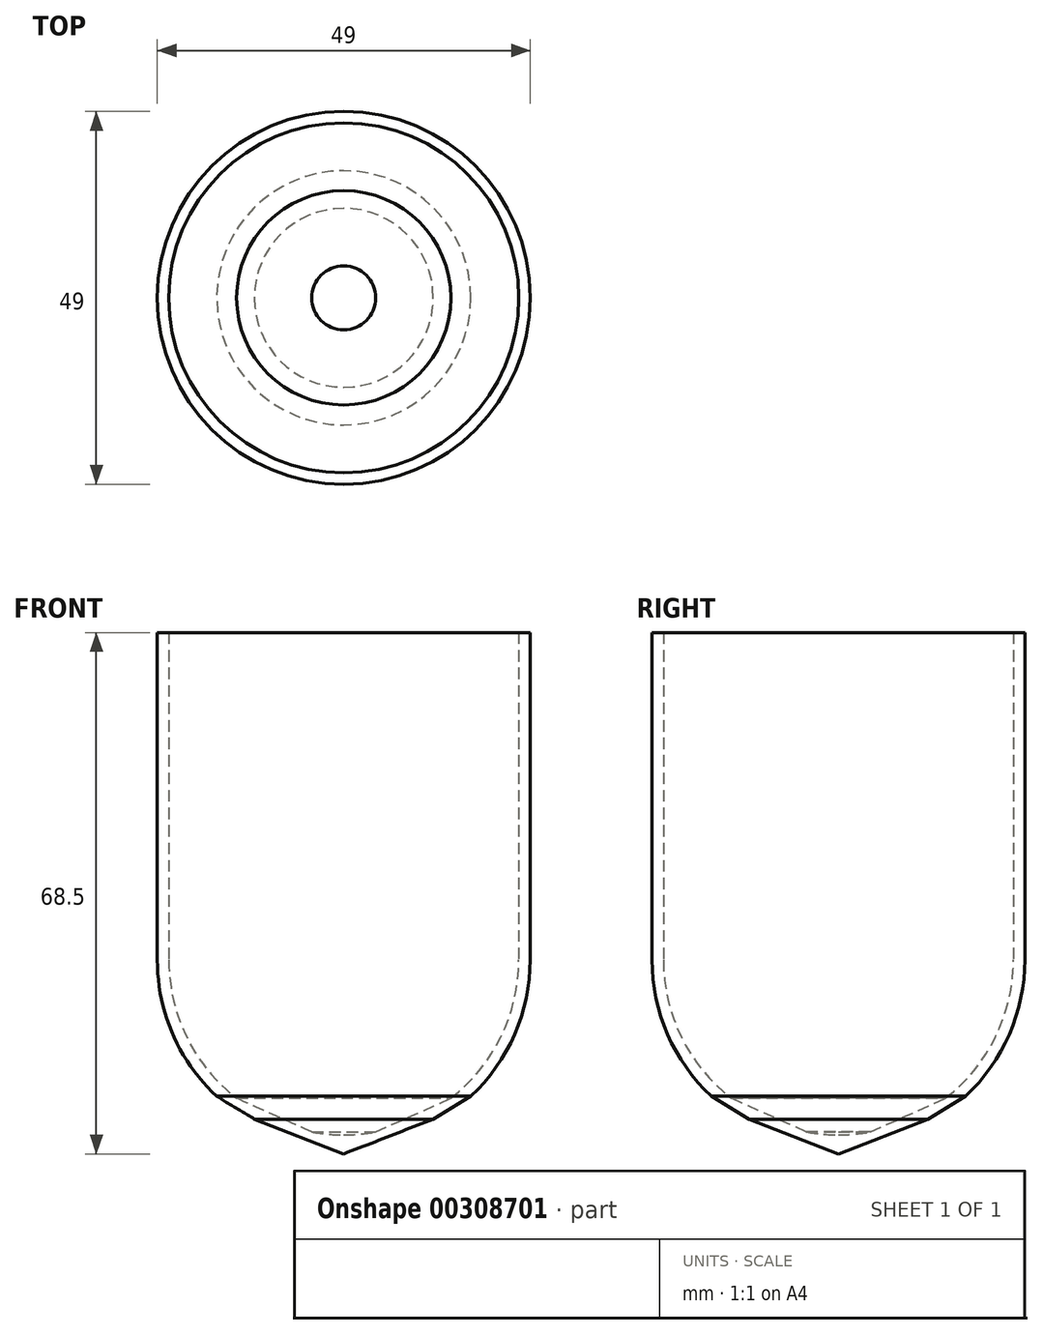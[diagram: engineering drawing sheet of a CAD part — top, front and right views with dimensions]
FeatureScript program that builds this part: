
annotation { "Feature Type Name" : "Feature", "Feature Type Description" : "" }
export const myFeature = defineFeature(function(context is Context, id is Id, definition is map)
    precondition{}
    {
        {
            var Q0;
            Q0=qCreatedBy(makeId("Front.planeOp"),FACE);
            var sketch = newSketch(context, id + "F0", { "sketchPlane" : qUnion([Q0])});
            skLineSegment(sketch, "E0", {"start": v(0, 0) * mm, "end": v(23, 0) * mm, "construction": true});
            skArc(sketch, "E1", {"start": v(0, -23) * mm, "mid": v(16.26, -16.26) * mm, "end": v(23, 0) * mm});
            skArc(sketch, "E2.0", {"start": v(0, -24.5) * mm, "mid": v(17.32, -17.32) * mm, "end": v(24.5, 0) * mm});
            skLineSegment(sketch, "E3", {"start": v(0, -23) * mm, "end": v(0, -24.5) * mm});
            skLineSegment(sketch, "E4", {"start": v(23, 0) * mm, "end": v(24.5, 0) * mm, "construction": true});
            skLineSegment(sketch, "E5", {"start": v(0, -23) * mm, "end": v(0, 0) * mm, "construction": true});
            skLineSegment(sketch, "E6", {"start": v(0, 0) * mm, "end": v(0, 48) * mm, "construction": true});
            skLineSegment(sketch, "E7", {"start": v(23, 0) * mm, "end": v(23, 48) * mm});
            skLineSegment(sketch, "E8", {"start": v(23, 48) * mm, "end": v(24.5, 48) * mm, "construction": true});
            skLineSegment(sketch, "E9", {"start": v(24.5, 48) * mm, "end": v(24.5, 0) * mm});
            skLineSegment(sketch, "E10", {"start": v(24.5, 0) * mm, "end": v(25.5, 0) * mm, "construction": true});
            skLineSegment(sketch, "E11", {"start": v(25.5, 0) * mm, "end": v(32.5, 0) * mm, "construction": true});
            skLineSegment(sketch, "E12", {"start": v(24.5, 48) * mm, "end": v(24.5, 43) * mm});
            skLineSegment(sketch, "E13", {"start": v(24.5, 43) * mm, "end": v(23, 43) * mm});
            skLineSegment(sketch, "E14", {"start": v(0, -24.5) * mm, "end": v(0, -25.5) * mm});
            skLineSegment(sketch, "E15", {"start": v(0, -25.5) * mm, "end": v(11.76, -20.92) * mm});
            skLineSegment(sketch, "E16", {"start": v(11.76, -20.92) * mm, "end": v(16.7, -17.92) * mm});
            skLineSegment(sketch, "E17", {"start": v(4.2, -22.61) * mm, "end": v(14.08, -18.19) * mm});
            skSolve(sketch);
        }
        {
            var Q0;
            {var subQ0=sQuery(id+"F0.wireOp",EDGE,"E17");Q0=makeQuery(id+"F0.imprint","IMPRINT",FACE,{"disambiguationData":[TD([[makeQuery(id+"F0.imprint","IMPRINT",EDGE,{"derivedFrom":subQ0}),-1.0]])]});}
            var Q1;
            {var subQ5=sQuery(id+"F0.wireOp",EDGE,"E3");Q1=makeQuery(id+"F0.imprint","IMPRINT",FACE,{"disambiguationData":[TD([[makeQuery(id+"F0.imprint","IMPRINT",EDGE,{"derivedFrom":subQ5}),1.0]])]});}
            var Q2;
            {var subQ0=sQuery(id+"F0.wireOp",EDGE,"E14");Q2=makeQuery(id+"F0.imprint","IMPRINT",FACE,{"disambiguationData":[TD([[makeQuery(id+"F0.imprint","IMPRINT",EDGE,{"derivedFrom":subQ0}),1.0]])]});}
            var Q3;
            Q3=sQuery(id+"F0.wireOp",EDGE,"E6");
            revolve(context, id + "F1", {"entities" : qUnion([Q0, Q1, Q2]), "axis" : qUnion([Q3]), "revolveType" : RevolveType.FULL});
        }
    });
